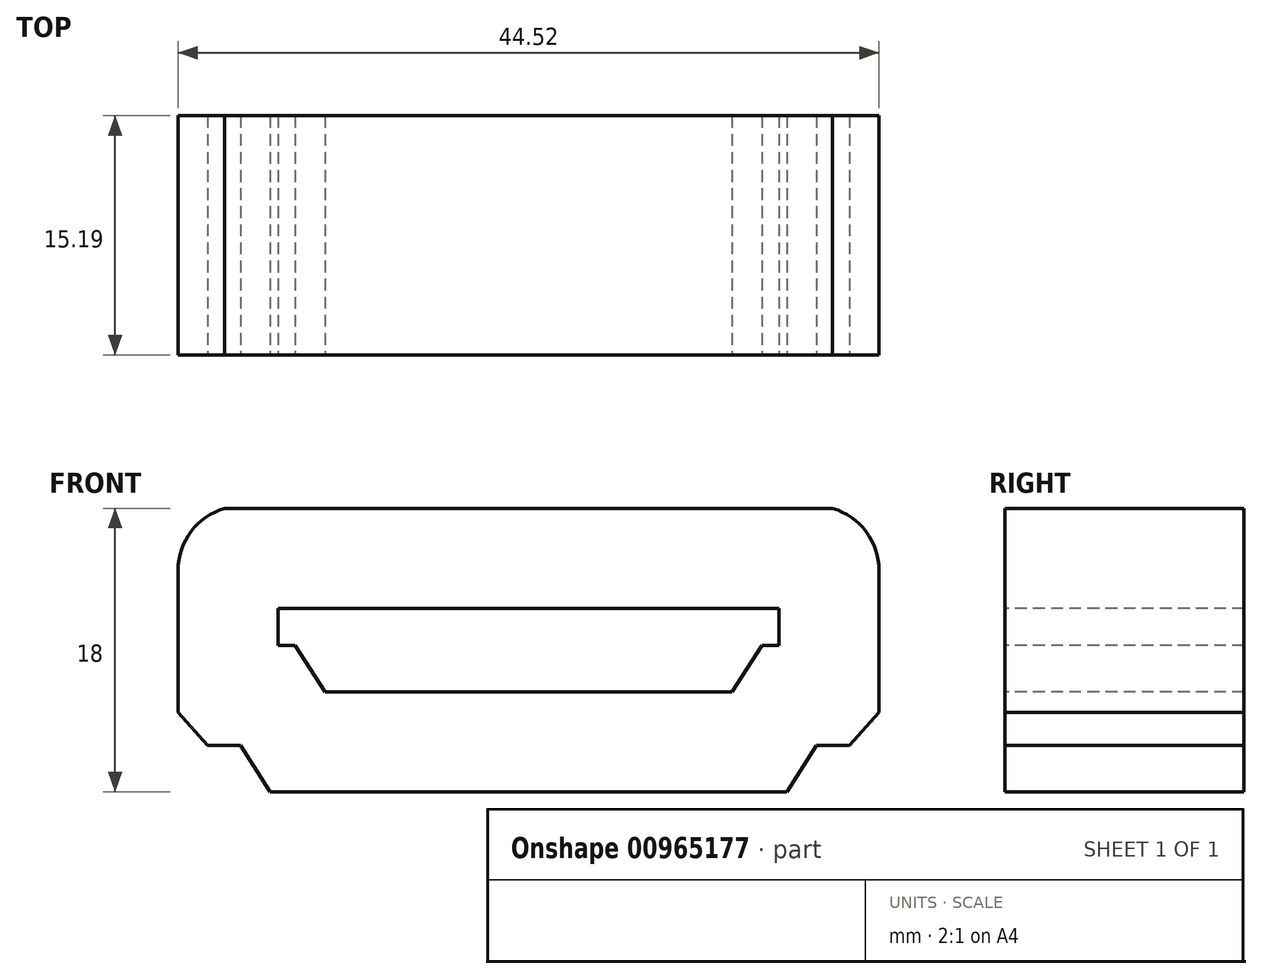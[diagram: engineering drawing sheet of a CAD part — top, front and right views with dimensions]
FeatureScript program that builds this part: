
annotation { "Feature Type Name" : "Feature", "Feature Type Description" : "" }
export const myFeature = defineFeature(function(context is Context, id is Id, definition is map)
    precondition{}
    {
        {
            var Q0;
            Q0=qCreatedBy(makeId("Front.planeOp"),FACE);
            var sketch = newSketch(context, id + "F0", { "sketchPlane" : qUnion([Q0])});
            skLineSegment(sketch, "E0", {"start": v(0, -14.07) * mm, "end": v(-16.4, -14.07) * mm});
            skLineSegment(sketch, "E1", {"start": v(-16.4, -14.07) * mm, "end": v(-18.29, -11.14) * mm});
            skLineSegment(sketch, "E2", {"start": v(-18.29, -11.14) * mm, "end": v(-20.38, -11.14) * mm});
            skLineSegment(sketch, "E3", {"start": v(-20.38, -11.14) * mm, "end": v(-22.26, -9.04) * mm});
            skLineSegment(sketch, "E4", {"start": v(-22.26, -9.04) * mm, "end": v(-22.26, 0) * mm});
            skArc(sketch, "E5", {"start": v(-19.32, 3.93) * mm, "mid": v(-21.44, 2.45) * mm, "end": v(-22.26, 0) * mm});
            skLineSegment(sketch, "E6", {"start": v(-19.32, 3.93) * mm, "end": v(0, 3.93) * mm});
            skLineSegment(sketch, "E7.MirrorCS", {"start": v(19.32, 3.93) * mm, "end": v(0, 3.93) * mm});
            skArc(sketch, "E8.MirrorCS", {"start": v(19.32, 3.93) * mm, "mid": v(21.44, 2.45) * mm, "end": v(22.26, 0) * mm});
            skLineSegment(sketch, "E9.MirrorCS", {"start": v(22.26, -9.04) * mm, "end": v(22.26, 0) * mm});
            skLineSegment(sketch, "E10.MirrorCS", {"start": v(20.38, -11.14) * mm, "end": v(22.26, -9.04) * mm});
            skLineSegment(sketch, "E11.MirrorCS", {"start": v(18.29, -11.14) * mm, "end": v(20.38, -11.14) * mm});
            skLineSegment(sketch, "E12.MirrorCS", {"start": v(16.4, -14.07) * mm, "end": v(18.29, -11.14) * mm});
            skLineSegment(sketch, "E13.MirrorCS", {"start": v(0, -14.07) * mm, "end": v(16.4, -14.07) * mm});
            skLineSegment(sketch, "E14.0", {"start": v(0, -7.72) * mm, "end": v(12.93, -7.72) * mm});
            skLineSegment(sketch, "E14.1", {"start": v(12.93, -7.72) * mm, "end": v(14.82, -4.79) * mm});
            skLineSegment(sketch, "E14.2", {"start": v(0, -7.72) * mm, "end": v(-12.93, -7.72) * mm});
            skLineSegment(sketch, "E14.3", {"start": v(14.82, -4.79) * mm, "end": v(15.91, -4.79) * mm});
            skLineSegment(sketch, "E14.4", {"start": v(15.91, -4.79) * mm, "end": v(15.91, -2.42) * mm});
            skLineSegment(sketch, "E14.5", {"start": v(15.91, -2.42) * mm, "end": v(0, -2.42) * mm});
            skLineSegment(sketch, "E14.6", {"start": v(-12.93, -7.72) * mm, "end": v(-14.82, -4.79) * mm});
            skLineSegment(sketch, "E14.7", {"start": v(-14.82, -4.79) * mm, "end": v(-15.91, -4.79) * mm});
            skLineSegment(sketch, "E14.8", {"start": v(-15.91, -4.79) * mm, "end": v(-15.91, -2.42) * mm});
            skLineSegment(sketch, "E14.9", {"start": v(-15.91, -2.42) * mm, "end": v(0, -2.42) * mm});
            skSolve(sketch);
        }
        {
            var Q0;
            Q0 = qConstructionFilter(qBodyType(qCreatedBy(id + "F0" ,EDGE), BodyType.WIRE), ConstructionObject.NO);
            extrude(context, id + "F1", {"bodyType" : ToolBodyType.SURFACE, "surfaceEntities" : qUnion([Q0]), "depth" : 15.2 * mm, "offsetDistance" : 25.4 * mm});
        }
    });
